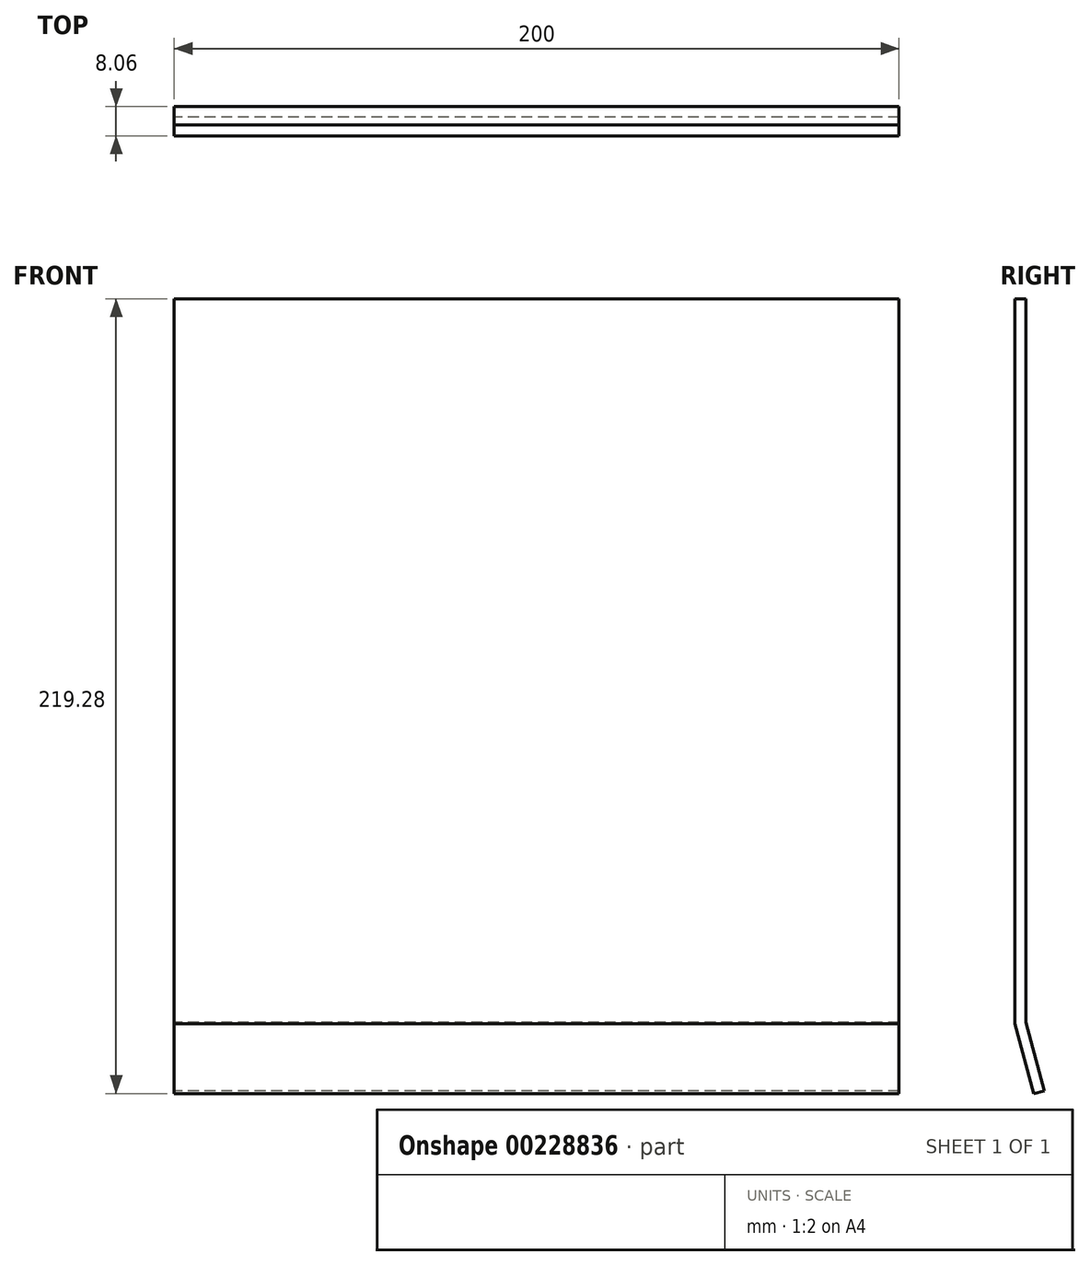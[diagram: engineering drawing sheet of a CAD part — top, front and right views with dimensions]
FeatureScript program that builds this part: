
annotation { "Feature Type Name" : "Feature", "Feature Type Description" : "" }
export const myFeature = defineFeature(function(context is Context, id is Id, definition is map)
    precondition{}
    {
        {
            var Q0;
            Q0=qCreatedBy(makeId("Right.planeOp"),FACE);
            var sketch = newSketch(context, id + "F0", { "sketchPlane" : qUnion([Q0])});
            skLineSegment(sketch, "E0", {"start": v(0, 0) * mm, "end": v(0, 0) * mm});
            skLineSegment(sketch, "E1", {"start": v(0, 0) * mm, "end": v(5.17, -19.28) * mm});
            skLineSegment(sketch, "E2", {"start": v(0, 0) * mm, "end": v(0, -23.7) * mm, "construction": true});
            skLineSegment(sketch, "E3", {"start": v(0, 0) * mm, "end": v(-13.3, 0) * mm, "construction": true});
            skLineSegment(sketch, "E4", {"start": v(0, 0) * mm, "end": v(0, 200) * mm});
            skLineSegment(sketch, "E5", {"start": v(0, 200) * mm, "end": v(3, 200) * mm});
            skLineSegment(sketch, "E6", {"start": v(3, 200) * mm, "end": v(3, 0.4) * mm});
            skLineSegment(sketch, "E7", {"start": v(3, 0.4) * mm, "end": v(8.06, -18.5) * mm});
            skLineSegment(sketch, "E8", {"start": v(8.06, -18.5) * mm, "end": v(5.17, -19.28) * mm});
            skSolve(sketch);
        }
        {
            var Q0;
            Q0 = qSketchRegion(id + "F0", true);
            extrude(context, id + "F1", {"entities" : qUnion([Q0]), "depth" : 200 * mm});
        }
    });
